# Revit family: WashbasinUnit-100cm-WithOneDrawer-WithInfinityWashbasin-Vitra-MetropoleSeries-58195+58196+61288
name_source: partatom
category: Furniture Systems
revit_build: Autodesk Revit 2017 (Build: 20160225_1515(x64)
units: mm (PartAtom-declared; Revit-internal decimal feet)

## family parameters
Cut with Voids When Loaded = No
Host = Face
OmniClass Number = 23.40.00.00
OmniClass Title = Equipment and Furnishings
Part Type = Normal
Room Calculation Point = No
Round Connector Dimension = Use Diameter
Shared = Yes

## types (3) — shared parameters
BIMobject category = Bathroom compound units
Brand = VitrA
Default Elevation = 660 mm
Description = Metropole Washbasin Unit - 100cm - with One drawers
Design country = Turkey
IFC Classification = Furniture
Main Material = Wood
Manufacturer = Vitra
Manufacturer name = Vitra
Masterformat 2014 Code = 13 42 13
Masterformat 2014 Description = Bathroom Unit Modules
Mounting type = Wall Hung
NBS Referans Code = 35-75-08
NBS Referans Description = Bathroom Cabinets
Nominal Depth (mm) = 515 mm
Nominal Height (mm) = 418 mm
Nominal Width (mm) = 990 mm
OmniClass Code = 23-31 25 13
OmniClass Description = Bathroom Cabinets
Product certification = https://www.vitraglobal.com
Product family = Metropole
Product group = Washbasin Unit
Third Material = Metal
UNSPSC Description = Bathroom Cabinets
URL = https://vitraglobal.com
Uniclass 1.4 Code = L8241
Uniclass 1.4 Description = Bathroom Cabinets
Uniclass 2.0 Code = PR-35-75-08
Uniclass 2.0 Description = Bathroom Cabinets
Uniclass 2015 Code = Pr_40_20_93
Uniclass 2015 Name = Wash basins, sinks and troughs
Uniformat II Code = E20
Uniformat II Description = FURNISHINGS
Warranty Period (Year) = 2
Youtube = https://www.youtube.com

## per-type parameters (varying)
| type | Article No. (default) | Color | Model | Primary Material | Product SKU | Product data url | Product url | Secondary Material | Technical description |
| WashbasinUnit-100cm-WithOneDrawer-WithVanityBasin-Vitra-MetropoleSeries-58195 | 58195 | Plum Tree | 58195 | Plum Tree | 58195 | https://www.bimobject.com | https://www.vitraglobal.com | Black Acrylic Glass | https://www.vitraglobal.com |
| WashbasinUnit-100cm-WithOneDrawer-WithVanityBasin-Vitra-MetropoleSeries-58196 | 58196 | High Gloss White | 58196 | High Gloss White | 58196 |  | https://www.vitraglobal.com | White Acrylic Glass | https://www.vitraglobal.com |
| WashbasinUnit-100cm-WithOneDrawer-WithVanityBasin-Vitra-MetropoleSeries-61288 | 61288 | Silver Oak | 61288 | Silver Oak | 61288 |  | https://vitraglobal.com | White Acrylic Glass | https://vitraglobal.com |

## geometry (parser evidence)
native form markers: Sweep x2
no freeform markers — native parametric forms only
